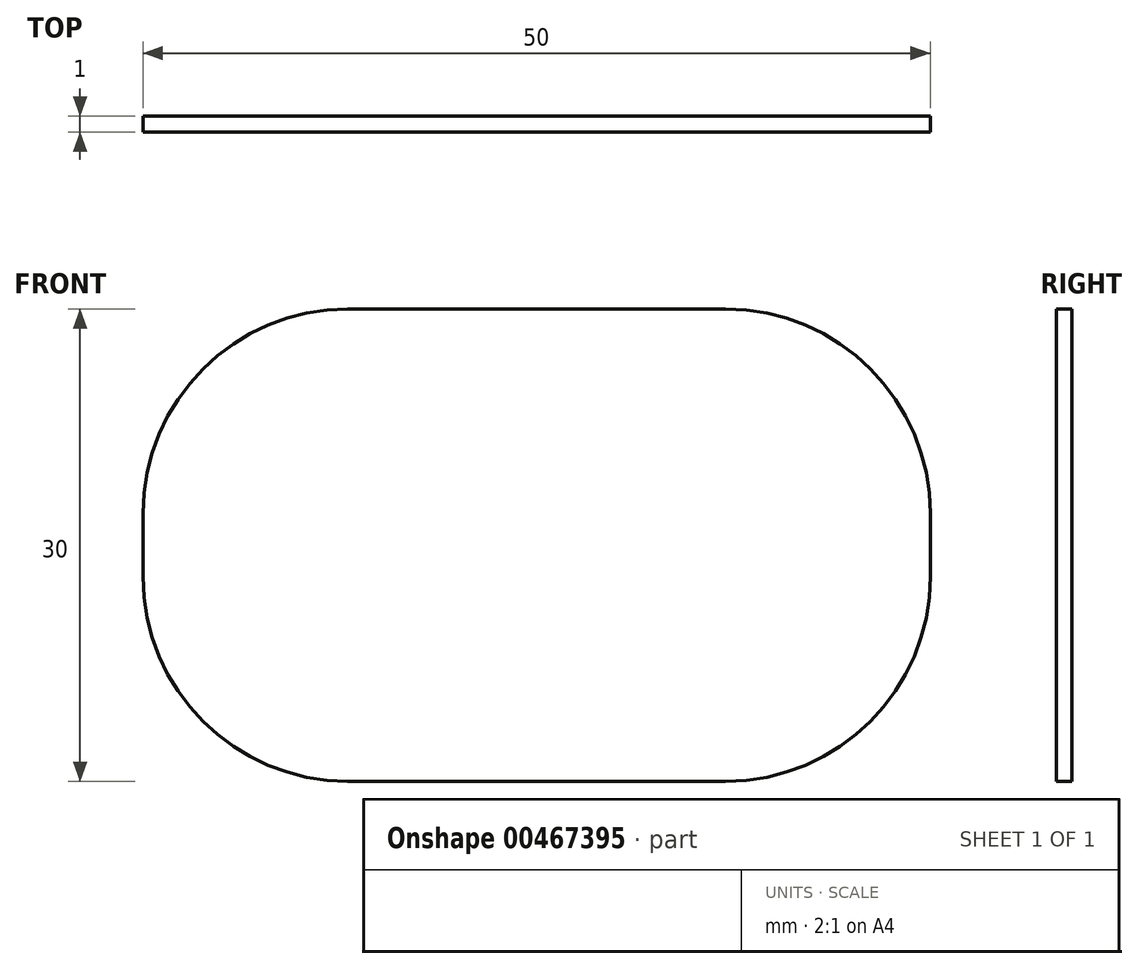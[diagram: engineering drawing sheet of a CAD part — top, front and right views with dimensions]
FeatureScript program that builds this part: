
annotation { "Feature Type Name" : "Feature", "Feature Type Description" : "" }
export const myFeature = defineFeature(function(context is Context, id is Id, definition is map)
    precondition{}
    {
        {
            var Q0;
            Q0=qCreatedBy(makeId("Front.planeOp"),FACE);
            var sketch = newSketch(context, id + "F0", { "sketchPlane" : qUnion([Q0])});
            skLineSegment(sketch, "E0.bottom", {"start": v(13, 0) * mm, "end": v(37, 0) * mm});
            skLineSegment(sketch, "E0.top", {"start": v(13, -30) * mm, "end": v(37, -30) * mm});
            skLineSegment(sketch, "E0.left", {"start": v(0, -13) * mm, "end": v(0, -17) * mm});
            skLineSegment(sketch, "E0.right", {"start": v(50, -13) * mm, "end": v(50, -17) * mm});
            skPoint(sketch, "E1.visualSharp", {"position": v(0, 0) * mm});
            skArc(sketch, "E1.filletArc", {"start": v(13, 0) * mm, "mid": v(3.8, -3.8) * mm, "end": v(0, -13) * mm});
            skPoint(sketch, "E2.visualSharp", {"position": v(0, -30) * mm});
            skArc(sketch, "E2.filletArc", {"start": v(0, -17) * mm, "mid": v(3.8, -26.2) * mm, "end": v(13, -30) * mm});
            skPoint(sketch, "E3.visualSharp", {"position": v(50, 0) * mm});
            skArc(sketch, "E3.filletArc", {"start": v(50, -13) * mm, "mid": v(46.2, -3.8) * mm, "end": v(37, 0) * mm});
            skPoint(sketch, "E4.visualSharp", {"position": v(50, -30) * mm});
            skArc(sketch, "E4.filletArc", {"start": v(37, -30) * mm, "mid": v(46.2, -26.2) * mm, "end": v(50, -17) * mm});
            skSolve(sketch);
        }
        {
            var Q0;
            Q0=makeQuery(id+"F0.imprint","IMPRINT",FACE,{"disambiguationData":[TD([[makeQuery(id+"F0.imprint","IMPRINT",EDGE,{"derivedFrom":sQuery(id+"F0.wireOp",EDGE,"E0.bottom")}),-1.0]])]});
            extrude(context, id + "F1", {"entities" : qUnion([Q0]), "depth" : 1 * mm, "offsetDistance" : 25 * mm});
        }
    });
